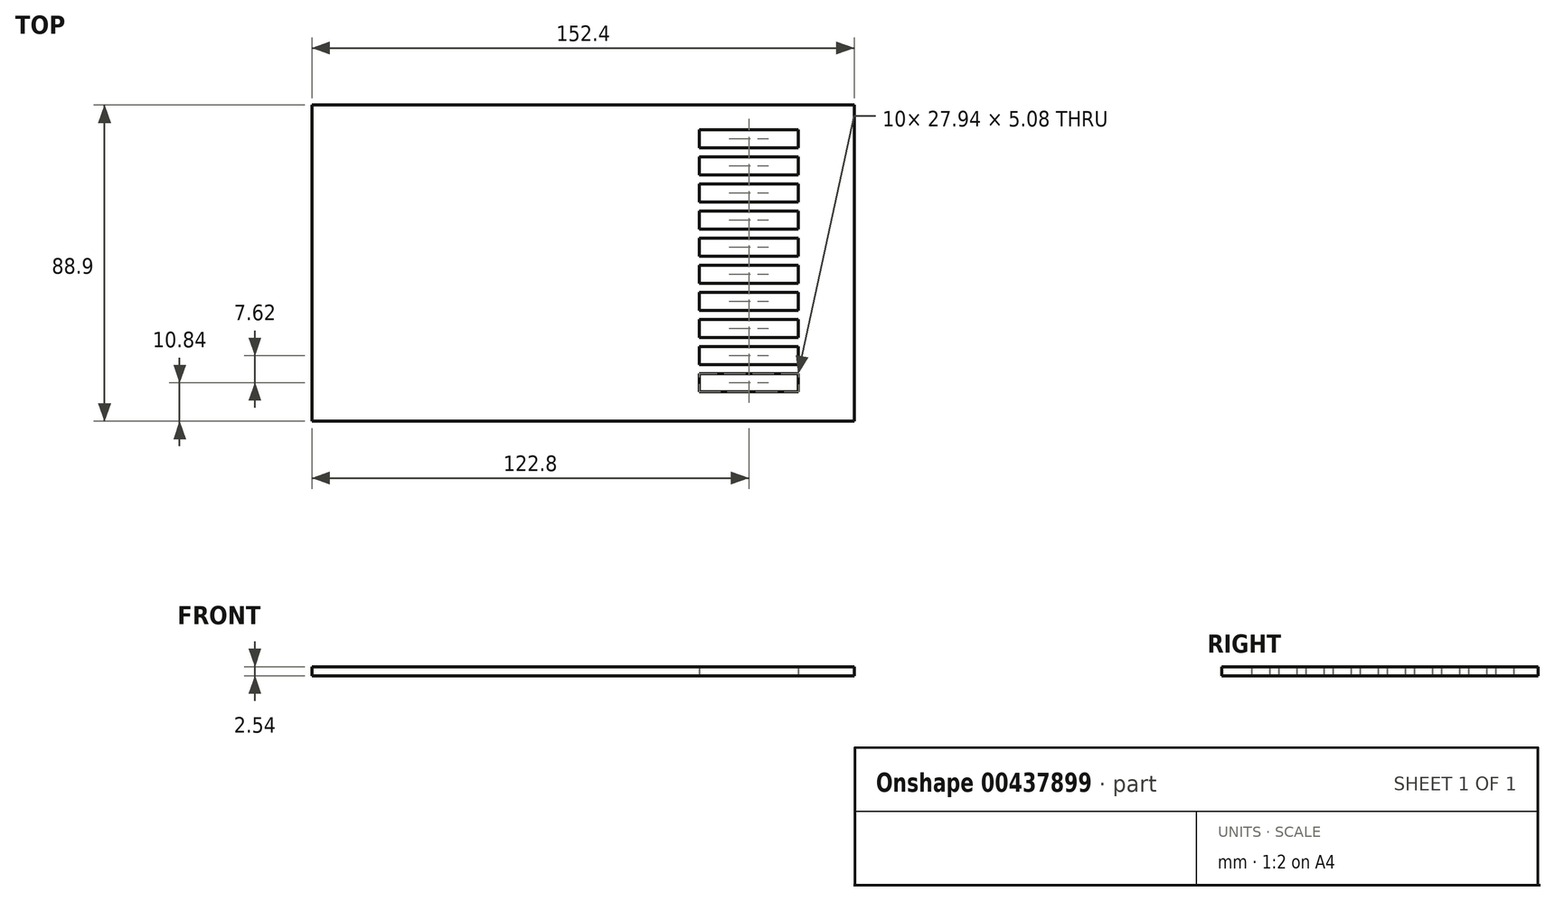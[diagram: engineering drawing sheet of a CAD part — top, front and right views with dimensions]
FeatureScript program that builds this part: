
annotation { "Feature Type Name" : "Feature", "Feature Type Description" : "" }
export const myFeature = defineFeature(function(context is Context, id is Id, definition is map)
    precondition{}
    {
        {
            var Q0;
            Q0=qCreatedBy(makeId("Top.planeOp"),FACE);
            var sketch = newSketch(context, id + "F0", { "sketchPlane" : qUnion([Q0])});
            skLineSegment(sketch, "E0.bottom", {"start": v(-38.26, 65.36) * mm, "end": v(114.14, 65.36) * mm});
            skLineSegment(sketch, "E0.top", {"start": v(-38.26, -23.54) * mm, "end": v(114.14, -23.54) * mm});
            skLineSegment(sketch, "E0.left", {"start": v(-38.26, 65.36) * mm, "end": v(-38.26, -23.54) * mm});
            skLineSegment(sketch, "E0.right", {"start": v(114.14, 65.36) * mm, "end": v(114.14, -23.54) * mm});
            skLineSegment(sketch, "E1.bottom", {"start": v(70.57, 58.42) * mm, "end": v(98.5, 58.42) * mm});
            skLineSegment(sketch, "E1.top", {"start": v(70.57, -15.24) * mm, "end": v(98.5, -15.24) * mm});
            skLineSegment(sketch, "E1.left", {"start": v(70.57, 58.42) * mm, "end": v(70.57, -15.24) * mm});
            skLineSegment(sketch, "E1.right", {"start": v(98.5, 58.42) * mm, "end": v(98.5, -15.24) * mm});
            skLineSegment(sketch, "E2.bottom", {"start": v(98.5, 58.42) * mm, "end": v(98.5, 58.42) * mm});
            skLineSegment(sketch, "E3.bottom", {"start": v(70.57, 20.32) * mm, "end": v(98.5, 20.32) * mm});
            skLineSegment(sketch, "E3.top", {"start": v(70.57, 15.24) * mm, "end": v(98.5, 15.24) * mm});
            skLineSegment(sketch, "E3.left", {"start": v(70.57, 20.32) * mm, "end": v(70.57, 15.24) * mm});
            skLineSegment(sketch, "E3.right", {"start": v(98.5, 20.32) * mm, "end": v(98.5, 15.24) * mm});
            skLineSegment(sketch, "E4.bottom", {"start": v(70.57, 12.7) * mm, "end": v(98.5, 12.7) * mm});
            skLineSegment(sketch, "E4.top", {"start": v(70.57, 7.62) * mm, "end": v(98.5, 7.62) * mm});
            skLineSegment(sketch, "E4.left", {"start": v(70.57, 12.7) * mm, "end": v(70.57, 7.62) * mm});
            skLineSegment(sketch, "E4.right", {"start": v(98.5, 12.7) * mm, "end": v(98.5, 7.62) * mm});
            skLineSegment(sketch, "E5.top", {"start": v(70.57, 5.08) * mm, "end": v(98.5, 5.08) * mm});
            skLineSegment(sketch, "E5.left", {"start": v(70.57, 21.59) * mm, "end": v(70.57, 5.08) * mm});
            skLineSegment(sketch, "E5.right", {"start": v(98.5, 20.32) * mm, "end": v(98.5, 5.08) * mm});
            skLineSegment(sketch, "E6.bottom", {"start": v(98.5, -2.54) * mm, "end": v(70.57, -2.54) * mm});
            skLineSegment(sketch, "E6.top", {"start": v(98.5, 0) * mm, "end": v(70.57, 0) * mm});
            skLineSegment(sketch, "E6.left", {"start": v(98.5, 0) * mm, "end": v(98.5, -2.54) * mm});
            skLineSegment(sketch, "E6.right", {"start": v(70.57, 0) * mm, "end": v(70.57, -2.54) * mm});
            skLineSegment(sketch, "E7.bottom", {"start": v(70.57, -7.62) * mm, "end": v(98.5, -7.62) * mm});
            skLineSegment(sketch, "E7.top", {"start": v(70.57, -10.16) * mm, "end": v(98.5, -10.16) * mm});
            skLineSegment(sketch, "E7.left", {"start": v(70.57, -7.62) * mm, "end": v(70.57, -10.16) * mm});
            skLineSegment(sketch, "E7.right", {"start": v(98.5, -7.62) * mm, "end": v(98.5, -10.16) * mm});
            skLineSegment(sketch, "E8.bottom", {"start": v(70.57, 27.94) * mm, "end": v(98.5, 27.94) * mm});
            skLineSegment(sketch, "E8.top", {"start": v(70.57, 22.86) * mm, "end": v(98.5, 22.86) * mm});
            skLineSegment(sketch, "E8.left", {"start": v(70.57, 27.94) * mm, "end": v(70.57, 22.86) * mm});
            skLineSegment(sketch, "E8.right", {"start": v(98.5, 27.94) * mm, "end": v(98.5, 22.86) * mm});
            skLineSegment(sketch, "E9.bottom", {"start": v(98.5, 30.48) * mm, "end": v(70.57, 30.48) * mm});
            skLineSegment(sketch, "E9.top", {"start": v(98.5, 35.56) * mm, "end": v(70.57, 35.56) * mm});
            skLineSegment(sketch, "E9.left", {"start": v(98.5, 30.48) * mm, "end": v(98.5, 35.56) * mm});
            skLineSegment(sketch, "E9.right", {"start": v(70.57, 30.48) * mm, "end": v(70.57, 35.56) * mm});
            skLineSegment(sketch, "E10.bottom", {"start": v(70.57, 38.1) * mm, "end": v(98.5, 38.1) * mm});
            skLineSegment(sketch, "E10.left", {"start": v(70.57, 38.1) * mm, "end": v(70.57, 35.42) * mm});
            skLineSegment(sketch, "E10.right", {"start": v(98.5, 38.1) * mm, "end": v(98.5, 38.07) * mm});
            skLineSegment(sketch, "E11.left", {"start": v(98.5, 44.1) * mm, "end": v(98.5, 42.36) * mm});
            skLineSegment(sketch, "E11.right", {"start": v(70.57, 44.1) * mm, "end": v(70.57, 42.36) * mm});
            skLineSegment(sketch, "E12", {"start": v(70.57, 43.18) * mm, "end": v(98.5, 43.18) * mm});
            skLineSegment(sketch, "E13", {"start": v(70.57, 45.72) * mm, "end": v(98.5, 45.72) * mm});
            skLineSegment(sketch, "E14", {"start": v(70.57, 50.8) * mm, "end": v(98.5, 50.8) * mm});
            skLineSegment(sketch, "E15", {"start": v(70.57, 53.34) * mm, "end": v(98.5, 53.34) * mm});
            skSolve(sketch);
        }
        {
            var Q0;
            Q0=makeQuery(id+"F0.imprint","IMPRINT",FACE,{"disambiguationData":[TD([[makeQuery(id+"F0.imprint","IMPRINT",EDGE,{"derivedFrom":sQuery(id+"F0.wireOp",EDGE,"E0.bottom")}),-1.0]])]});
            var Q1;
            {var subQ0=sQuery(id+"F0.wireOp",EDGE,"E4.bottom");Q1=makeQuery(id+"F0.imprint","IMPRINT",FACE,{"disambiguationData":[TD([[makeQuery(id+"F0.imprint","IMPRINT",EDGE,{"derivedFrom":subQ0}),1.0]])]});}
            var Q2;
            {var subQ0=sQuery(id+"F0.wireOp",EDGE,"E4.top");Q2=makeQuery(id+"F0.imprint","IMPRINT",FACE,{"disambiguationData":[TD([[makeQuery(id+"F0.imprint","IMPRINT",EDGE,{"derivedFrom":subQ0}),-1.0]])]});}
            var Q3;
            Q3=makeQuery(id+"F0.imprint","IMPRINT",FACE,{"disambiguationData":[TD([[makeQuery(id+"F0.imprint","IMPRINT",EDGE,{"derivedFrom":sQuery(id+"F0.wireOp",EDGE,"E6.bottom")}),-1.0]])]});
            var Q4;
            Q4=makeQuery(id+"F0.imprint","IMPRINT",FACE,{"disambiguationData":[TD([[makeQuery(id+"F0.imprint","IMPRINT",EDGE,{"derivedFrom":sQuery(id+"F0.wireOp",EDGE,"E7.bottom")}),-1.0]])]});
            var Q5;
            {var subQ3=sQuery(id+"F0.wireOp",EDGE,"E12");Q5=makeQuery(id+"F0.imprint","IMPRINT",FACE,{"disambiguationData":[TD([[makeQuery(id+"F0.imprint","IMPRINT",EDGE,{"derivedFrom":subQ3}),1.0]])]});}
            var Q6;
            {var subQ0=sQuery(id+"F0.wireOp",EDGE,"E14");Q6=makeQuery(id+"F0.imprint","IMPRINT",FACE,{"disambiguationData":[TD([[makeQuery(id+"F0.imprint","IMPRINT",EDGE,{"derivedFrom":subQ0}),1.0]])]});}
            var Q7;
            {var subQ0=sQuery(id+"F0.wireOp",EDGE,"E3.bottom");Q7=makeQuery(id+"F0.imprint","IMPRINT",FACE,{"disambiguationData":[TD([[makeQuery(id+"F0.imprint","IMPRINT",EDGE,{"derivedFrom":subQ0}),1.0]])]});}
            var Q8;
            {var subQ0=sQuery(id+"F0.wireOp",EDGE,"E8.bottom");Q8=makeQuery(id+"F0.imprint","IMPRINT",FACE,{"disambiguationData":[TD([[makeQuery(id+"F0.imprint","IMPRINT",EDGE,{"derivedFrom":subQ0}),1.0]])]});}
            var Q9;
            {var subQ1=sQuery(id+"F0.wireOp",EDGE,"E9.top");Q9=makeQuery(id+"F0.imprint","IMPRINT",FACE,{"disambiguationData":[TD([[makeQuery(id+"F0.imprint","IMPRINT",EDGE,{"derivedFrom":subQ1}),-1.0]])]});}
            extrude(context, id + "F1", {"entities" : qUnion([Q0, Q1, Q2, Q3, Q4, Q5, Q6, Q7, Q8, Q9]), "depth" : 2.54 * mm});
        }
    });
